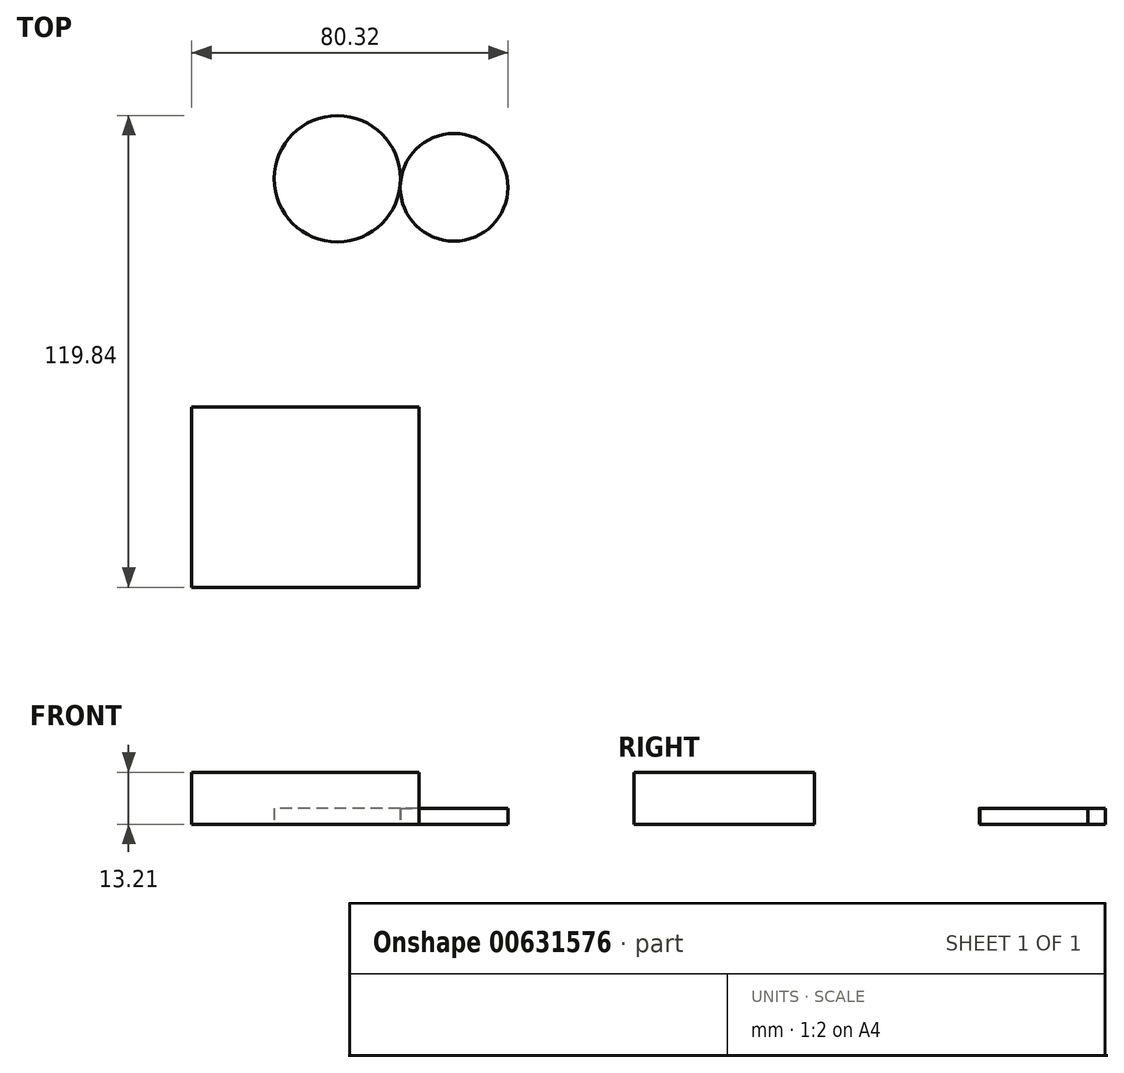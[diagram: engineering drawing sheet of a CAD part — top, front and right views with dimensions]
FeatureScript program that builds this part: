
annotation { "Feature Type Name" : "Feature", "Feature Type Description" : "" }
export const myFeature = defineFeature(function(context is Context, id is Id, definition is map)
    precondition{}
    {
        {
            var Q0;
            Q0=qCreatedBy(makeId("Top.planeOp"),FACE);
            var sketch = newSketch(context, id + "F0", { "sketchPlane" : qUnion([Q0])});
            skLineSegment(sketch, "E0.bottom", {"start": v(-35, -17.17) * mm, "end": v(22.78, -17.17) * mm});
            skLineSegment(sketch, "E0.top", {"start": v(-35, -62.99) * mm, "end": v(22.78, -62.99) * mm});
            skLineSegment(sketch, "E0.left", {"start": v(-35, -17.17) * mm, "end": v(-35, -62.99) * mm});
            skLineSegment(sketch, "E0.right", {"start": v(22.78, -17.17) * mm, "end": v(22.78, -62.99) * mm});
            skCircle(sketch, "E1", {"center": v(1.98, 40.8) * mm, "radius": 16.05 * mm});
            skCircle(sketch, "E2", {"center": v(31.63, 38.62) * mm, "radius": 13.68 * mm});
            skSolve(sketch);
        }
        {
            var Q0;
            Q0=makeQuery(id+"F0.imprint","IMPRINT",FACE,{"disambiguationData":[TD([[makeQuery(id+"F0.imprint","IMPRINT",EDGE,{"derivedFrom":sQuery(id+"F0.wireOp",EDGE,"E0.bottom")}),-1.0]])]});
            extrude(context, id + "F1", {"entities" : qUnion([Q0]), "depth" : 13.2 * mm, "offsetDistance" : 25.4 * mm});
        }
        {
            var Q0;
            Q0=makeQuery(id+"F0.imprint","IMPRINT",FACE,{"disambiguationData":[TD([[makeQuery(id+"F0.imprint","IMPRINT",EDGE,{"derivedFrom":sQuery(id+"F0.wireOp",EDGE,"E2")}),1.0]])]});
            var Q1;
            Q1=makeQuery(id+"F0.imprint","IMPRINT",FACE,{"disambiguationData":[TD([[makeQuery(id+"F0.imprint","IMPRINT",EDGE,{"derivedFrom":sQuery(id+"F0.wireOp",EDGE,"E1")}),1.0]])]});
            extrude(context, id + "F2", {"entities" : qUnion([Q0, Q1]), "depth" : 4.06 * mm, "offsetDistance" : 25.4 * mm});
        }
    });
